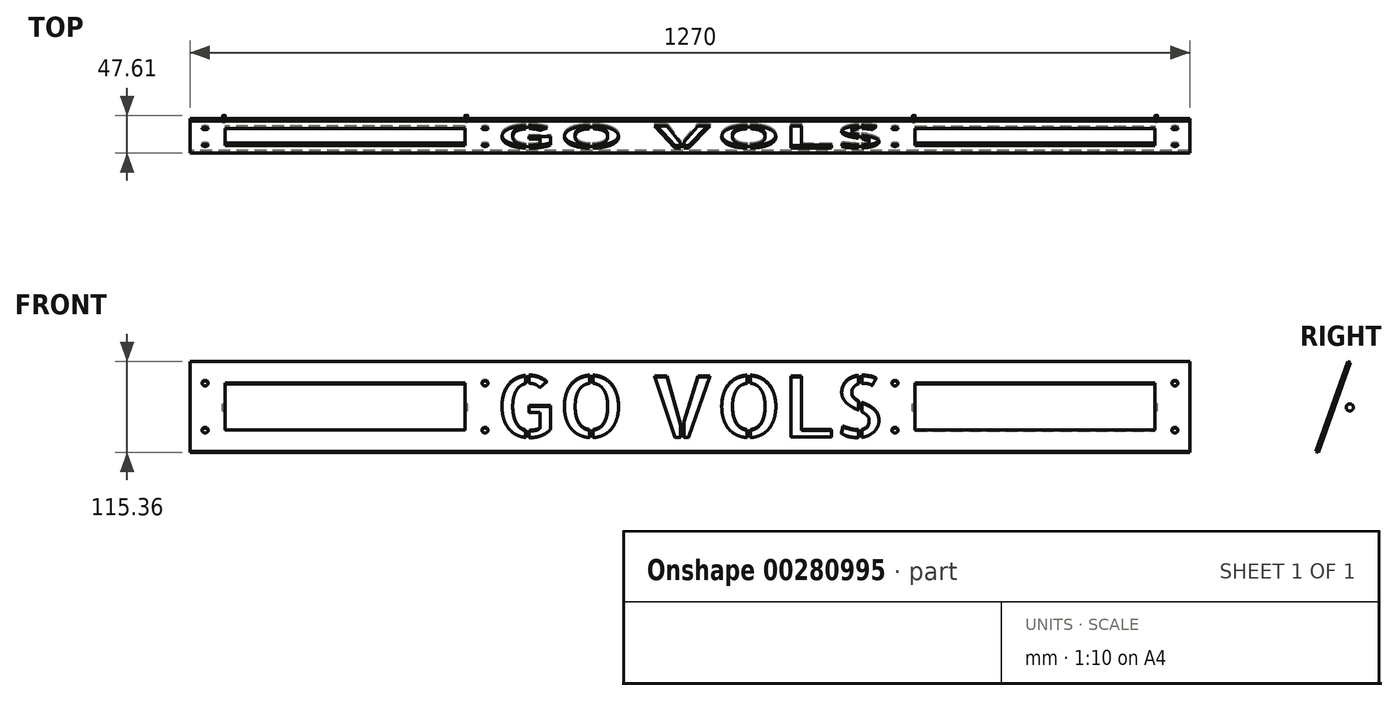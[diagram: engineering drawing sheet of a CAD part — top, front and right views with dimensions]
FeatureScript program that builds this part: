
annotation { "Feature Type Name" : "Feature", "Feature Type Description" : "" }
export const myFeature = defineFeature(function(context is Context, id is Id, definition is map)
    precondition{}
    {
        {
            var Q0;
            Q0=qCreatedBy(makeId("Right.planeOp"),FACE);
            var sketch = newSketch(context, id + "F0", { "sketchPlane" : qUnion([Q0])});
            skLineSegment(sketch, "E0", {"start": v(0, 0) * mm, "end": v(40.64, 114.3) * mm});
            skLineSegment(sketch, "E1", {"start": v(40.64, 114.3) * mm, "end": v(43.63, 113.24) * mm});
            skLineSegment(sketch, "E2", {"start": v(43.63, 113.24) * mm, "end": v(3, -1.06) * mm});
            skLineSegment(sketch, "E3", {"start": v(0, 0) * mm, "end": v(3, -1.06) * mm});
            skSolve(sketch);
        }
        {
            var Q0;
            Q0 = qSketchRegion(id + "F0", true);
            extrude(context, id + "F1", {"entities" : qUnion([Q0]), "endBound" : BoundingType.SYMMETRIC, "depth" : 1270 * mm});
        }
        {
            var Q0;
            Q0=makeQuery(id+"F1.opExtrude","SWEPT_FACE",FACE,{"disambiguationData":[OSD([sQuery(id+"F0.wireOp",EDGE,"E0")])]});
            var sketch = newSketch(context, id + "F2", { "sketchPlane" : qUnion([Q0])});
            skText(sketch, "E4", { "text": "GO VOLS", "fontName": "AllertaStencil-Regular.ttf"});
            skLineSegment(sketch, "E5", {"start": v(0, 0) * mm, "end": v(0, 19.38) * mm, "construction": true});
            const initialGuessF2  = {"E4": [-0.2477, 0.01938, 1, 0, 0.08255]};
            skSetInitialGuess(sketch, initialGuessF2);
            skSolve(sketch);
        }
        {
            var Q0;
            Q0 = qSketchRegion(id + "F2", true);
            var Q1;
            Q1=makeQuery(id+"F1.opExtrude","SWEPT_FACE",FACE,{"disambiguationData":[OSD([sQuery(id+"F0.wireOp",EDGE,"E2")])]});
            extrude(context, id + "F3", {"entities" : qUnion([Q0]), "operationType" : NewBodyOperationType.REMOVE, "endBound" : BoundingType.UP_TO_SURFACE, "oppositeDirection" : true, "endBoundEntityFace" : qUnion([Q1]), "depth" : 25.4 * mm});
        }
        {
            var Q0;
            Q0=makeQuery(id+"F1.opExtrude","SWEPT_FACE",FACE,{"disambiguationData":[OSD([sQuery(id+"F0.wireOp",EDGE,"E0")])]});
            var sketch = newSketch(context, id + "F4", { "sketchPlane" : qUnion([Q0])});
            skLineSegment(sketch, "E6.bottom", {"start": v(285.75, 92.4) * mm, "end": v(590.55, 92.4) * mm});
            skLineSegment(sketch, "E6.top", {"start": v(285.75, 28.9) * mm, "end": v(590.55, 28.9) * mm});
            skLineSegment(sketch, "E6.left", {"start": v(285.75, 92.4) * mm, "end": v(285.75, 28.9) * mm});
            skLineSegment(sketch, "E6.right", {"start": v(590.55, 92.4) * mm, "end": v(590.55, 28.9) * mm});
            skLineSegment(sketch, "E7", {"start": v(0, 0) * mm, "end": v(0, -235.78) * mm, "construction": true});
            skLineSegment(sketch, "E8.MirrorCS", {"start": v(-285.75, 92.4) * mm, "end": v(-285.75, 28.9) * mm});
            skLineSegment(sketch, "E9.MirrorCS", {"start": v(-285.75, 92.4) * mm, "end": v(-590.55, 92.4) * mm});
            skLineSegment(sketch, "E10.MirrorCS", {"start": v(-285.75, 28.9) * mm, "end": v(-590.55, 28.9) * mm});
            skLineSegment(sketch, "E11.MirrorCS", {"start": v(-590.55, 92.4) * mm, "end": v(-590.55, 28.9) * mm});
            skSolve(sketch);
        }
        {
            var Q0;
            Q0 = qSketchRegion(id + "F4", true);
            var Q1;
            Q1=makeQuery(id+"F1.opExtrude","SWEPT_FACE",FACE,{"disambiguationData":[OSD([sQuery(id+"F0.wireOp",EDGE,"E2")])]});
            extrude(context, id + "F5", {"entities" : qUnion([Q0]), "operationType" : NewBodyOperationType.REMOVE, "endBound" : BoundingType.UP_TO_SURFACE, "oppositeDirection" : true, "endBoundEntityFace" : qUnion([Q1]), "depth" : 25.4 * mm});
        }
        {
            var Q0;
            Q0=makeQuery(id+"F1.opExtrude","SWEPT_FACE",FACE,{"disambiguationData":[OSD([sQuery(id+"F0.wireOp",EDGE,"E0")])]});
            var sketch = newSketch(context, id + "F6", { "sketchPlane" : qUnion([Q0])});
            skCircle(sketch, "E12", {"center": v(-615.95, 92.4) * mm, "radius": 3.81 * mm});
            skCircle(sketch, "E13", {"center": v(-615.95, 28.9) * mm, "radius": 3.81 * mm});
            skLineSegment(sketch, "E14", {"start": v(0, 0) * mm, "end": v(0, -156.15) * mm, "construction": true});
            skCircle(sketch, "E15.MirrorC", {"center": v(615.95, 92.4) * mm, "radius": 3.81 * mm});
            skCircle(sketch, "E16.MirrorC", {"center": v(615.95, 28.9) * mm, "radius": 3.81 * mm});
            skLineSegment(sketch, "E17", {"start": v(-438.15, 92.4) * mm, "end": v(-438.15, 175.13) * mm, "construction": true});
            skCircle(sketch, "E18.MirrorC", {"center": v(-260.35, 92.4) * mm, "radius": 3.81 * mm});
            skCircle(sketch, "E19.MirrorC", {"center": v(-260.35, 28.9) * mm, "radius": 3.81 * mm});
            skCircle(sketch, "E20.MirrorC", {"center": v(260.35, 92.4) * mm, "radius": 3.81 * mm});
            skCircle(sketch, "E21.MirrorC", {"center": v(260.35, 28.9) * mm, "radius": 3.81 * mm});
            skSolve(sketch);
        }
        {
            var Q0;
            Q0 = qSketchRegion(id + "F6", true);
            var Q1;
            Q1=makeQuery(id+"F1.opExtrude","SWEPT_FACE",FACE,{"disambiguationData":[OSD([sQuery(id+"F0.wireOp",EDGE,"E2")])]});
            extrude(context, id + "F7", {"entities" : qUnion([Q0]), "operationType" : NewBodyOperationType.REMOVE, "endBound" : BoundingType.UP_TO_SURFACE, "oppositeDirection" : true, "endBoundEntityFace" : qUnion([Q1]), "depth" : 25.4 * mm});
        }
        {
            var Q0;
            Q0=qCreatedBy(makeId("Right.planeOp"),FACE);
            var Q1;
            Q1=makeQuery(id+"F5.boolean.opBoolean","COPY",VERTEX,{"derivedFrom":makeQuery(id+"F5.opExtrude","CAP_VERTEX",VERTEX,{"disambiguationData":[OSD([sQuery(id+"F4.wireOp",EDGE,"E9.MirrorCS"),sQuery(id+"F4.wireOp",EDGE,"E11.MirrorCS")])],"isStart":true})});
            cPlane(context, id + "F8", {"entities" : qUnion([Q0, Q1]), "cplaneType" : CPlaneType.PLANE_POINT, "offset" : 25.4 * mm, "width" : 152.4 * mm, "height" : 152.4 * mm});
        }
        {
            var Q0;
            Q0=qCreatedBy(id+"F8.planeOp",FACE);
            var sketch = newSketch(context, id + "F9", { "sketchPlane" : qUnion([Q0])});
            skLineSegment(sketch, "E22", {"start": v(33.95, 86) * mm, "end": v(12.68, 26.17) * mm, "construction": true});
            skLineSegment(sketch, "E23", {"start": v(23.31, 56.09) * mm, "end": v(78.84, 56.09) * mm, "construction": true});
            skLineSegment(sketch, "E24", {"start": v(28.73, 71.33) * mm, "end": v(46.51, 71.33) * mm});
            skLineSegment(sketch, "E25", {"start": v(17.9, 40.85) * mm, "end": v(46.51, 40.85) * mm});
            skLineSegment(sketch, "E26", {"start": v(17.9, 40.85) * mm, "end": v(28.73, 71.33) * mm});
            skEllipticalArc(sketch, "E27", {});
            skCircle(sketch, "E28", {"center": v(43.16, 56.09) * mm, "radius": 4.45 * mm});
            const initialGuessF9  = {"E27": [0.043762006700694085, 0.047819336831427216, 0, -1, 0.01524, 0.009525, 0, 3.141592653589793]};
            skSetInitialGuess(sketch, initialGuessF9);
            skSolve(sketch);
        }
        {
            var Q0;
            Q0 = qSketchRegion(id + "F9", true);
            extrude(context, id + "F10", {"entities" : qUnion([Q0]), "oppositeDirection" : true, "depth" : 3.17 * mm});
        }
        {
            var Q0;
            Q0=makeQuery(id+"F5.boolean.opBoolean","COPY",FACE,{"derivedFrom":makeQuery(id+"F5.opExtrude","SWEPT_FACE",FACE,{"disambiguationData":[OSD([sQuery(id+"F4.wireOp",EDGE,"E11.MirrorCS")])]})});
            var Q1;
            Q1=makeQuery(id+"F5.boolean.opBoolean","COPY",FACE,{"derivedFrom":makeQuery(id+"F5.opExtrude","SWEPT_FACE",FACE,{"disambiguationData":[OSD([sQuery(id+"F4.wireOp",EDGE,"E8.MirrorCS")])]})});
            cPlane(context, id + "F11", {"entities" : qUnion([Q0, Q1]), "cplaneType" : CPlaneType.MID_PLANE, "offset" : 25.4 * mm, "width" : 152.4 * mm, "height" : 152.4 * mm});
        }
        {
            var Q0;
            Q0=makeQuery(id+"F10.opExtrude","SWEPT_BODY",BODY,{"disambiguationData":[OSD([sQuery(id+"F9.wireOp",EDGE,"E24"),sQuery(id+"F9.wireOp",EDGE,"E25"),sQuery(id+"F9.wireOp",EDGE,"E26"),sQuery(id+"F9.wireOp",EDGE,"E27"),sQuery(id+"F9.wireOp",EDGE,"E28")])]});
            var Q1;
            Q1=qCreatedBy(id+"F11.planeOp",FACE);
            mirror(context, id + "F12", {"entities" : qUnion([Q0]), "mirrorPlane" : qUnion([Q1])});
        }
        {
            var Q0;
            Q0=makeQuery(id+"F12.opPattern","COPY",BODY,{"derivedFrom":makeQuery(id+"F10.opExtrude","SWEPT_BODY",BODY,{"disambiguationData":[OSD([sQuery(id+"F9.wireOp",EDGE,"E24"),sQuery(id+"F9.wireOp",EDGE,"E25"),sQuery(id+"F9.wireOp",EDGE,"E26"),sQuery(id+"F9.wireOp",EDGE,"E27"),sQuery(id+"F9.wireOp",EDGE,"E28")])]}),"instanceName":"1"});
            var Q1;
            Q1=makeQuery(id+"F10.opExtrude","SWEPT_BODY",BODY,{"disambiguationData":[OSD([sQuery(id+"F9.wireOp",EDGE,"E24"),sQuery(id+"F9.wireOp",EDGE,"E25"),sQuery(id+"F9.wireOp",EDGE,"E26"),sQuery(id+"F9.wireOp",EDGE,"E27"),sQuery(id+"F9.wireOp",EDGE,"E28")])]});
            var Q2;
            Q2=qCreatedBy(makeId("Right.planeOp"),FACE);
            mirror(context, id + "F13", {"operationType" : NewBodyOperationType.ADD, "entities" : qUnion([Q0, Q1]), "mirrorPlane" : qUnion([Q2])});
        }
    });
